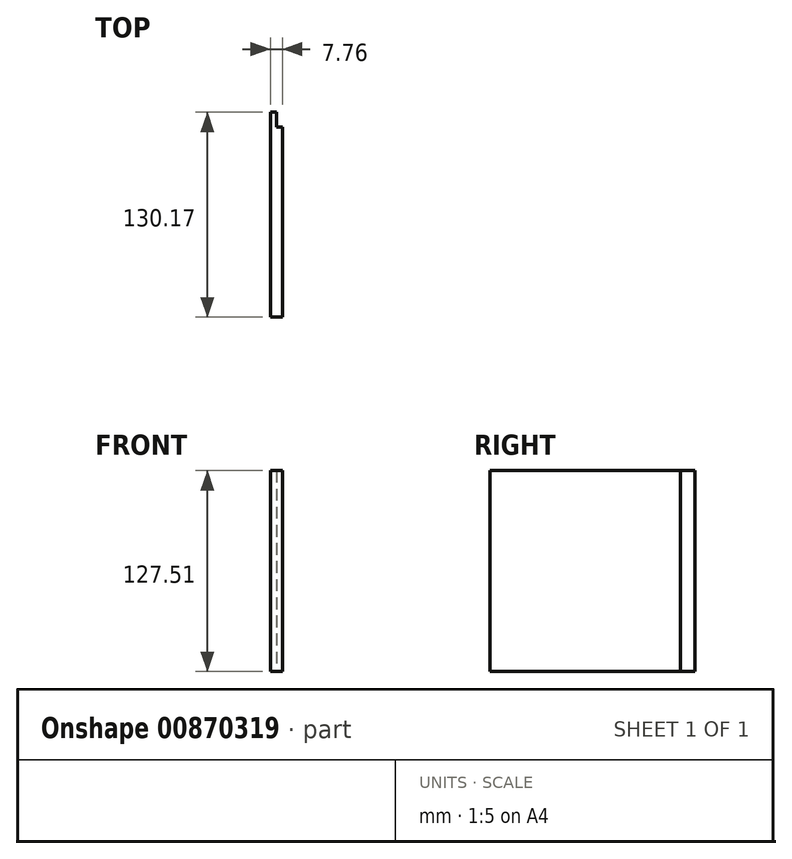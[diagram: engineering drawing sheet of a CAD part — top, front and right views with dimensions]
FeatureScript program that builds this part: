
annotation { "Feature Type Name" : "Feature", "Feature Type Description" : "" }
export const myFeature = defineFeature(function(context is Context, id is Id, definition is map)
    precondition{}
    {
        {
            var Q0;
            Q0=qCreatedBy(makeId("Top.planeOp"),FACE);
            var sketch = newSketch(context, id + "F0", { "sketchPlane" : qUnion([Q0])});
            skLineSegment(sketch, "E0.bottom", {"start": v(-111.48, -54.33) * mm, "end": v(-103.72, -54.33) * mm});
            skLineSegment(sketch, "E0.top", {"start": v(-111.48, 75.84) * mm, "end": v(-107.6, 75.84) * mm});
            skLineSegment(sketch, "E0.left", {"start": v(-111.48, -54.33) * mm, "end": v(-111.48, 75.84) * mm});
            skLineSegment(sketch, "E0.right", {"start": v(-103.72, -54.33) * mm, "end": v(-103.72, 66.56) * mm});
            skLineSegment(sketch, "E1", {"start": v(-107.6, 75.84) * mm, "end": v(-107.6, 66.56) * mm});
            skLineSegment(sketch, "E2", {"start": v(-107.6, 66.56) * mm, "end": v(-103.72, 66.56) * mm});
            skPoint(sketch, "E3.orphan", {"position": v(-103.72, 75.84) * mm});
            skSolve(sketch);
        }
        {
            var Q0;
            Q0=makeQuery(id+"F0.imprint","IMPRINT",FACE,{"disambiguationData":[TD([[makeQuery(id+"F0.imprint","IMPRINT",EDGE,{"derivedFrom":sQuery(id+"F0.wireOp",EDGE,"E0.bottom")}),1.0]])]});
            extrude(context, id + "F1", {"entities" : qUnion([Q0]), "depth" : 127.5 * mm, "offsetDistance" : 25.4 * mm});
        }
    });
